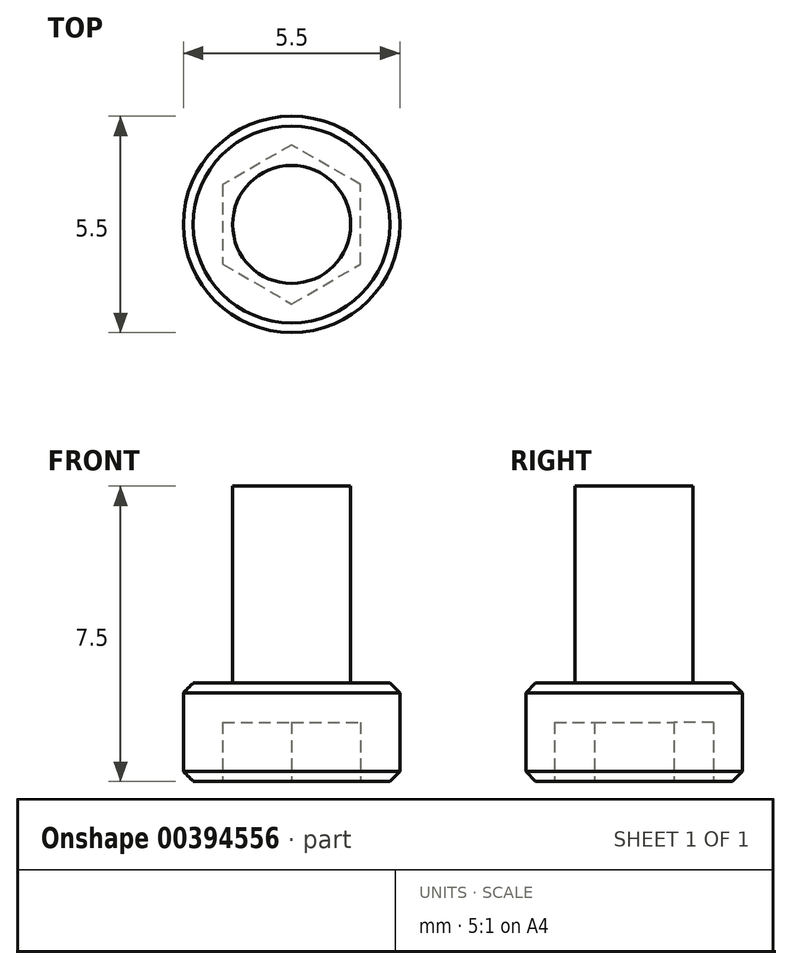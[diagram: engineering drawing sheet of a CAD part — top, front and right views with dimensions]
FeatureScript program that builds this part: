
annotation { "Feature Type Name" : "Feature", "Feature Type Description" : "" }
export const myFeature = defineFeature(function(context is Context, id is Id, definition is map)
    precondition{}
    {
        {
            var Q0;
            Q0=qCreatedBy(makeId("Top.planeOp"),FACE);
            var sketch = newSketch(context, id + "F0", { "sketchPlane" : qUnion([Q0])});
            skCircle(sketch, "E0", {"center": v(0, 0) * mm, "radius": 1.5 * mm});
            skSolve(sketch);
        }
        {
            var Q0;
            Q0 = qSketchRegion(id + "F0", true);
            extrude(context, id + "F1", {"entities" : qUnion([Q0]), "depth" : 5 * mm});
        }
        {
            var Q0;
            Q0=makeQuery(id+"F1.opExtrude","CAP_FACE",FACE,{"disambiguationData":[OSD([sQuery(id+"F0.wireOp",EDGE,"E0")])],"isStart":true});
            var sketch = newSketch(context, id + "F2", { "sketchPlane" : qUnion([Q0])});
            skCircle(sketch, "E1", {"center": v(0, 0) * mm, "radius": 2.75 * mm});
            skSolve(sketch);
        }
        {
            var Q0;
            Q0 = qSketchRegion(id + "F2", true);
            extrude(context, id + "F3", {"entities" : qUnion([Q0]), "operationType" : NewBodyOperationType.ADD, "depth" : 2.5 * mm});
        }
        {
            var Q0;
            Q0=makeQuery(id+"F3.opExtrude","CAP_FACE",FACE,{"disambiguationData":[OSD([sQuery(id+"F2.wireOp",EDGE,"E1")])],"isStart":false});
            var sketch = newSketch(context, id + "F4", { "sketchPlane" : qUnion([Q0])});
            skCircle(sketch, "E2.cCircle", {"center": v(0, 0) * mm, "radius": 1.75 * mm, "construction": true});
            skLineSegment(sketch, "E2.0", {"start": v(1.75, 1.01) * mm, "end": v(1.75, -1.01) * mm});
            skLineSegment(sketch, "E2.1", {"start": v(1.75, -1.01) * mm, "end": v(0, -2.02) * mm});
            skLineSegment(sketch, "E2.2", {"start": v(0, -2.02) * mm, "end": v(-1.75, -1.01) * mm});
            skLineSegment(sketch, "E2.3", {"start": v(-1.75, -1.01) * mm, "end": v(-1.75, 1.01) * mm});
            skLineSegment(sketch, "E2.4", {"start": v(-1.75, 1.01) * mm, "end": v(0, 2.02) * mm});
            skLineSegment(sketch, "E2.5", {"start": v(0, 2.02) * mm, "end": v(1.75, 1.01) * mm});
            skPoint(sketch, "E2.0.midPoint", {"position": v(1.75, 0) * mm});
            skSolve(sketch);
        }
        {
            var Q0;
            Q0 = qSketchRegion(id + "F4", true);
            extrude(context, id + "F5", {"entities" : qUnion([Q0]), "operationType" : NewBodyOperationType.REMOVE, "oppositeDirection" : true, "depth" : 1.5 * mm});
        }
        {
            var Q0;
            Q0=makeQuery(id+"F3.opExtrude","CAP_EDGE",EDGE,{"disambiguationData":[OSD([sQuery(id+"F2.wireOp",EDGE,"E1")])],"isStart":true});
            var Q1;
            Q1=makeQuery(id+"F3.opExtrude","CAP_EDGE",EDGE,{"disambiguationData":[OSD([sQuery(id+"F2.wireOp",EDGE,"E1")])],"isStart":false});
            chamfer(context, id + "F6", {"entities" : qUnion([Q0, Q1]), "width" : .25 * mm, "tangentPropagation" : true});
        }
    });
